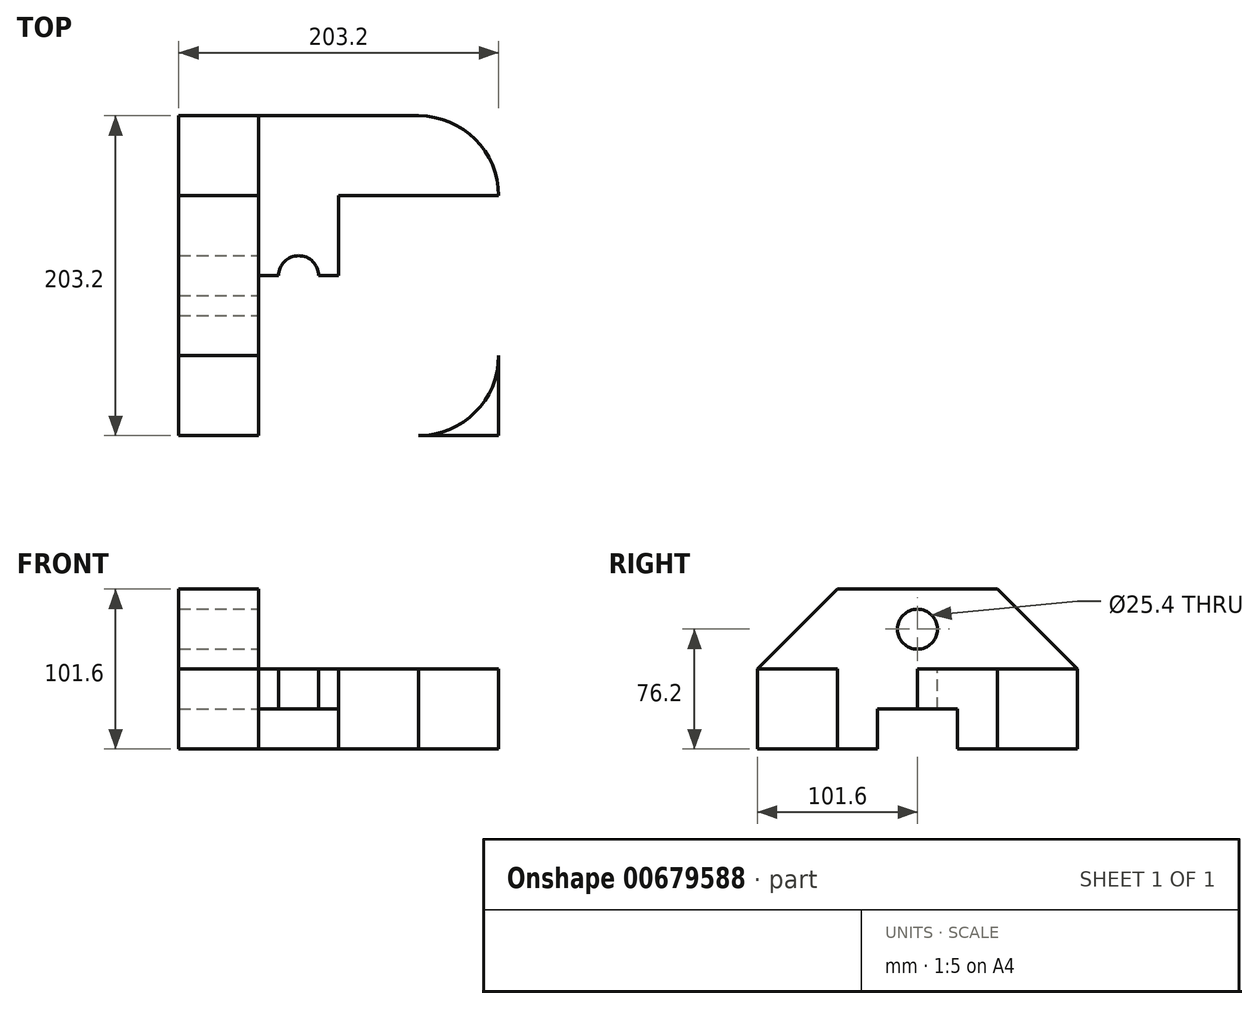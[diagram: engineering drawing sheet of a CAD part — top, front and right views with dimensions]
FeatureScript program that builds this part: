
annotation { "Feature Type Name" : "Feature", "Feature Type Description" : "" }
export const myFeature = defineFeature(function(context is Context, id is Id, definition is map)
    precondition{}
    {
        {
            var Q0;
            Q0=qCreatedBy(makeId("Front.planeOp"),FACE);
            var sketch = newSketch(context, id + "F0", { "sketchPlane" : qUnion([Q0])});
            skLineSegment(sketch, "E0", {"start": v(0, 0) * mm, "end": v(203.2, 0) * mm});
            skLineSegment(sketch, "E1", {"start": v(203.2, 0) * mm, "end": v(203.2, 50.8) * mm});
            skLineSegment(sketch, "E2", {"start": v(203.2, 50.8) * mm, "end": v(50.8, 50.8) * mm});
            skLineSegment(sketch, "E3", {"start": v(50.8, 50.8) * mm, "end": v(50.8, 101.6) * mm});
            skLineSegment(sketch, "E4", {"start": v(50.8, 101.6) * mm, "end": v(0, 101.6) * mm});
            skLineSegment(sketch, "E5", {"start": v(0, 101.6) * mm, "end": v(0, 0) * mm});
            skSolve(sketch);
        }
        {
            var Q0;
            Q0=makeQuery(id+"F0.imprint","IMPRINT",FACE,{"disambiguationData":[TD([[makeQuery(id+"F0.imprint","IMPRINT",EDGE,{"derivedFrom":sQuery(id+"F0.wireOp",EDGE,"E0")}),1.0]])]});
            extrude(context, id + "F1", {"entities" : qUnion([Q0]), "endBound" : BoundingType.SYMMETRIC, "depth" : 203.2 * mm, "offsetDistance" : 25.4 * mm});
        }
        {
            var Q0;
            Q0=makeQuery(id+"F1.opExtrude","SWEPT_FACE",FACE,{"disambiguationData":[OSD([sQuery(id+"F0.wireOp",EDGE,"E4")])]});
            var sketch = newSketch(context, id + "F2", { "sketchPlane" : qUnion([Q0])});
            skLineSegment(sketch, "E6", {"start": v(50.8, -101.6) * mm, "end": v(203.2, -101.6) * mm});
            skLineSegment(sketch, "E7", {"start": v(203.2, -101.6) * mm, "end": v(203.2, 50.8) * mm});
            skLineSegment(sketch, "E8", {"start": v(152.4, 101.6) * mm, "end": v(50.8, 101.6) * mm});
            skPoint(sketch, "E9.visualSharp", {"position": v(203.2, 101.6) * mm});
            skArc(sketch, "E9.filletArc", {"start": v(203.2, 50.8) * mm, "mid": v(188.32, 86.72) * mm, "end": v(152.4, 101.6) * mm});
            skArc(sketch, "E10.MirrorCS", {"start": v(203.2, -50.8) * mm, "mid": v(188.32, -86.72) * mm, "end": v(152.4, -101.6) * mm});
            skLineSegment(sketch, "E11", {"start": v(203.2, -50.8) * mm, "end": v(101.6, -50.8) * mm});
            skLineSegment(sketch, "E12", {"start": v(101.6, -50.8) * mm, "end": v(101.6, 50.8) * mm});
            skLineSegment(sketch, "E13", {"start": v(101.6, 50.8) * mm, "end": v(203.2, 50.8) * mm});
            skLineSegment(sketch, "E14", {"start": v(0, 0) * mm, "end": v(25.4, 0) * mm});
            skLineSegment(sketch, "E15", {"start": v(25.4, 0) * mm, "end": v(50.8, 0) * mm});
            skLineSegment(sketch, "E16", {"start": v(50.8, 0) * mm, "end": v(76.2, 0) * mm});
            skLineSegment(sketch, "E17", {"start": v(76.2, 0) * mm, "end": v(101.6, 0) * mm});
            skCircle(sketch, "E18", {"center": v(76.2, 0) * mm, "radius": 12.7 * mm});
            skLineSegment(sketch, "E19", {"start": v(152.4, 101.6) * mm, "end": v(203.2, 101.6) * mm});
            skLineSegment(sketch, "E20", {"start": v(203.2, 101.6) * mm, "end": v(203.2, 50.8) * mm});
            skSolve(sketch);
        }
        {
            var Q0;
            Q0=makeQuery(id+"F1.opExtrude","SWEPT_FACE",FACE,{"disambiguationData":[OSD([sQuery(id+"F0.wireOp",EDGE,"E1")])]});
            var sketch = newSketch(context, id + "F3", { "sketchPlane" : qUnion([Q0])});
            skLineSegment(sketch, "E21", {"start": v(-101.6, 50.8) * mm, "end": v(-101.6, 101.6) * mm});
            skLineSegment(sketch, "E22", {"start": v(-101.6, 101.6) * mm, "end": v(-50.8, 101.6) * mm});
            skLineSegment(sketch, "E23", {"start": v(-50.8, 101.6) * mm, "end": v(0, 101.6) * mm});
            skLineSegment(sketch, "E24", {"start": v(0, 101.6) * mm, "end": v(50.8, 101.6) * mm});
            skLineSegment(sketch, "E25", {"start": v(50.8, 101.6) * mm, "end": v(101.6, 101.6) * mm});
            skLineSegment(sketch, "E26", {"start": v(101.6, 101.6) * mm, "end": v(101.6, 50.8) * mm});
            skLineSegment(sketch, "E27", {"start": v(101.6, 50.8) * mm, "end": v(50.8, 50.8) * mm});
            skLineSegment(sketch, "E28", {"start": v(50.8, 50.8) * mm, "end": v(0, 50.8) * mm});
            skLineSegment(sketch, "E29", {"start": v(0, 50.8) * mm, "end": v(-50.8, 50.8) * mm});
            skLineSegment(sketch, "E30", {"start": v(-50.8, 50.8) * mm, "end": v(-101.6, 50.8) * mm});
            skLineSegment(sketch, "E31", {"start": v(0, 101.6) * mm, "end": v(0, 76.2) * mm});
            skLineSegment(sketch, "E32", {"start": v(0, 76.2) * mm, "end": v(0, 50.8) * mm});
            skLineSegment(sketch, "E33", {"start": v(-101.6, 0) * mm, "end": v(-50.8, 0) * mm});
            skLineSegment(sketch, "E34", {"start": v(-50.8, 0) * mm, "end": v(0, 0) * mm});
            skLineSegment(sketch, "E35", {"start": v(0, 0) * mm, "end": v(50.8, 0) * mm});
            skLineSegment(sketch, "E36", {"start": v(50.8, 0) * mm, "end": v(101.6, 0) * mm});
            skLineSegment(sketch, "E37", {"start": v(101.6, 0) * mm, "end": v(101.6, 50.8) * mm});
            skLineSegment(sketch, "E38", {"start": v(-25.4, 0) * mm, "end": v(-25.4, 25.4) * mm});
            skLineSegment(sketch, "E39", {"start": v(-25.4, 25.4) * mm, "end": v(25.4, 25.4) * mm});
            skPoint(sketch, "E39.endSnap0", {"position": v(25.4, 0) * mm});
            skLineSegment(sketch, "E40", {"start": v(25.4, 25.4) * mm, "end": v(25.4, 0) * mm});
            skCircle(sketch, "E41", {"center": v(0, 76.2) * mm, "radius": 12.7 * mm});
            skLineSegment(sketch, "E42", {"start": v(-101.6, 50.8) * mm, "end": v(-50.8, 101.6) * mm});
            skLineSegment(sketch, "E43", {"start": v(50.8, 101.6) * mm, "end": v(101.6, 50.8) * mm});
            skSolve(sketch);
        }
        {
            var Q0;
            Q0=makeQuery(id+"F3.imprint","IMPRINT",FACE,{"disambiguationData":[TD([[makeQuery(id+"F3.imprint","IMPRINT",EDGE,{"derivedFrom":sQuery(id+"F3.wireOp",EDGE,"E21")}),-1.0]])]});
            var Q1;
            {var subQ0=sQuery(id+"F3.wireOp",EDGE,"E32");var subQ1=sQuery(id+"F3.wireOp",EDGE,"E31");var subQ2=makeQuery(id+"F3.imprint","INTERSECT",VERTEX,{"derivedFrom":[subQ1,subQ0]});Q1=makeQuery(id+"F3.imprint","IMPRINT",FACE,{"disambiguationData":[TD([[makeQuery(id+"F3.imprint","IMPRINT",EDGE,{"disambiguationData":[TD([[subQ2,1.0]])],"derivedFrom":subQ1}),1.0]])]});}
            var Q2;
            {var subQ0=sQuery(id+"F3.wireOp",EDGE,"E32");var subQ1=sQuery(id+"F3.wireOp",EDGE,"E31");var subQ2=makeQuery(id+"F3.imprint","INTERSECT",VERTEX,{"derivedFrom":[subQ1,subQ0]});Q2=makeQuery(id+"F3.imprint","IMPRINT",FACE,{"disambiguationData":[TD([[makeQuery(id+"F3.imprint","IMPRINT",EDGE,{"disambiguationData":[TD([[subQ2,1.0]])],"derivedFrom":subQ1}),-1.0]])]});}
            var Q3;
            Q3=makeQuery(id+"F3.imprint","IMPRINT",FACE,{"disambiguationData":[TD([[makeQuery(id+"F3.imprint","IMPRINT",EDGE,{"derivedFrom":sQuery(id+"F3.wireOp",EDGE,"E25")}),-1.0]])]});
            var Q4;
            {var subQ4=sQuery(id+"F3.wireOp",EDGE,"E38");Q4=makeQuery(id+"F3.imprint","IMPRINT",FACE,{"disambiguationData":[TD([[makeQuery(id+"F3.imprint","IMPRINT",EDGE,{"derivedFrom":subQ4}),-1.0]])]});}
            extrude(context, id + "F4", {"entities" : qUnion([Q0, Q1, Q2, Q3, Q4]), "operationType" : NewBodyOperationType.REMOVE, "endBound" : BoundingType.SYMMETRIC, "oppositeDirection" : true, "depth" : 762 * mm, "offsetDistance" : 25.4 * mm});
        }
        {
            var Q0;
            {var subQ0=sQuery(id+"F2.wireOp",EDGE,"E17");var subQ1=sQuery(id+"F2.wireOp",EDGE,"E16");var subQ2=makeQuery(id+"F2.imprint","INTERSECT",VERTEX,{"derivedFrom":[subQ1,subQ0]});Q0=makeQuery(id+"F2.imprint","IMPRINT",FACE,{"disambiguationData":[TD([[makeQuery(id+"F2.imprint","IMPRINT",EDGE,{"disambiguationData":[TD([[subQ2,1.0]])],"derivedFrom":subQ1}),1.0]])]});}
            var Q1;
            {var subQ0=sQuery(id+"F2.wireOp",EDGE,"E17");var subQ1=sQuery(id+"F2.wireOp",EDGE,"E16");var subQ2=makeQuery(id+"F2.imprint","INTERSECT",VERTEX,{"derivedFrom":[subQ1,subQ0]});Q1=makeQuery(id+"F2.imprint","IMPRINT",FACE,{"disambiguationData":[TD([[makeQuery(id+"F2.imprint","IMPRINT",EDGE,{"disambiguationData":[TD([[subQ2,1.0]])],"derivedFrom":subQ1}),-1.0]])]});}
            var Q2;
            {var subQ3=sQuery(id+"F2.wireOp",EDGE,"E10.MirrorCS");Q2=makeQuery(id+"F2.imprint","IMPRINT",FACE,{"disambiguationData":[TD([[makeQuery(id+"F2.imprint","IMPRINT",EDGE,{"derivedFrom":subQ3}),1.0]])]});}
            var Q3;
            Q3=makeQuery(id+"F2.imprint","IMPRINT",FACE,{"disambiguationData":[TD([[makeQuery(id+"F2.imprint","IMPRINT",EDGE,{"derivedFrom":sQuery(id+"F2.wireOp",EDGE,"E9.filletArc")}),-1.0]])]});
            var Q4;
            {var subQ3=sQuery(id+"F2.wireOp",EDGE,"E11");Q4=makeQuery(id+"F2.imprint","IMPRINT",FACE,{"disambiguationData":[TD([[makeQuery(id+"F2.imprint","IMPRINT",EDGE,{"derivedFrom":subQ3}),-1.0]])]});}
            extrude(context, id + "F5", {"entities" : qUnion([Q0, Q1, Q2, Q3, Q4]), "operationType" : NewBodyOperationType.REMOVE, "oppositeDirection" : true, "depth" : 1270 * mm, "offsetDistance" : 25.4 * mm});
        }
    });
